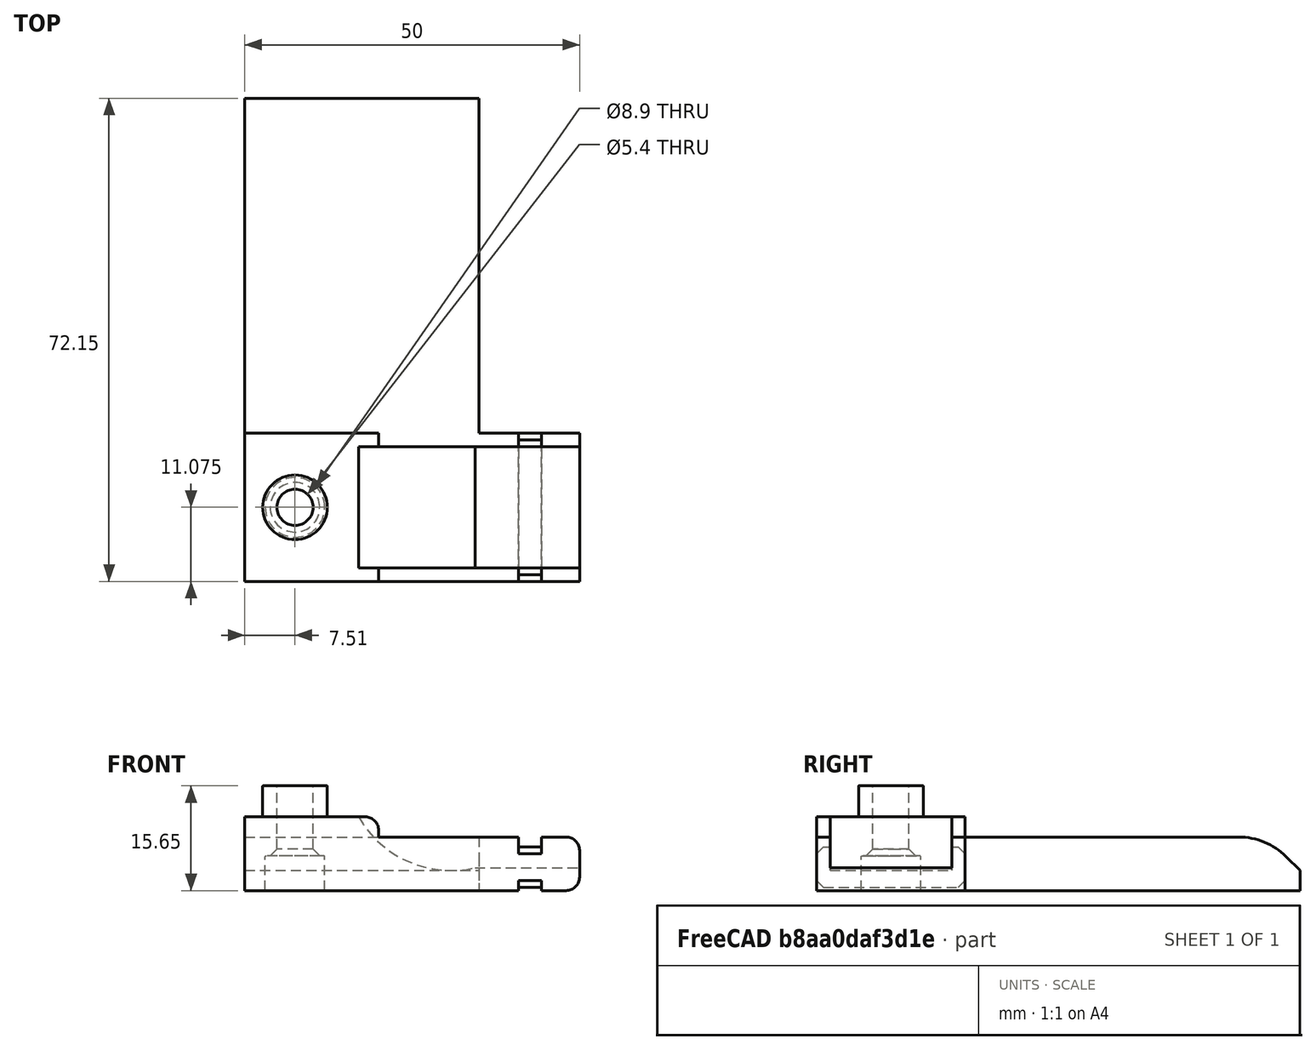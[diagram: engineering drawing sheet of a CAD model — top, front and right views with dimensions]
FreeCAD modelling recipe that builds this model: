
FCSTD DOCUMENT  (FreeCAD 0.19R24276 (Git))
Label: SoporteVelcroPowerBankCBR
License: All rights reserved
LicenseURL: http://en.wikipedia.org/wiki/All_rights_reserved
objects: TechDraw::DrawViewDimension×19, Part::Box×7, Part::MultiFuse×5, Part::Cylinder×4, Part::Offset×4, TechDraw::DrawProjGroupItem×3, Part::Cut×2, Part::Chamfer×2, Part::Fillet×2, TechDraw::DrawSVGTemplate×2, TechDraw::DrawViewPart×2, TechDraw::DrawPage×2, TechDraw::DrawProjGroup×1, TechDraw::DrawViewAnnotation×1
note: 26 computed .brp shape members not serialized (recipe doc carries the construction recipe); baked Part::Feature solids carry a one-line shape summary decoded from their .brp

FEATURE [Part::Cylinder] Cylinder
  Angle = 360
  AttacherType = Attacher::AttachEngine3D
  Height = 18.15
  Radius = 16
FEATURE [Part::Box] Box  label="Cube"
  AttacherType = Attacher::AttachEngine3D
  Height = 18.15
  Length = 17
  Placement = pos=(-30.835,0,0) rot=(0,0,1;0rad)
  Width = 8
FEATURE [Part::Box] Box001  label="Cube001"
  AttacherType = Attacher::AttachEngine3D
  Height = 18.15
  Length = 23
  Placement = pos=(3.4868,0,0) rot=(0,0,1;0rad)
  Width = 15.6
FEATURE [Part::Box] Box002  label="Cube002"
  AttacherType = Attacher::AttachEngine3D
  Height = 22.15
  Length = 50
  Placement = pos=(-30.84,11,-2) rot=(0,0,1;0rad)
  Width = 8
FEATURE [Part::Box] Box003  label="Cube003"
  AttacherType = Attacher::AttachEngine3D
  Height = 22.15
  Length = 20
  Placement = pos=(-30.84,8,-2) rot=(0,0,1;0rad)
  Width = 3
FEATURE [Part::Cylinder] Cylinder001
  Angle = 360
  AttacherType = Attacher::AttachEngine3D
  Height = 30
  Placement = pos=(-23.33,30,9.075) rot=(1,0,0;1.5708rad)
  Radius = 2.5
FEATURE [Part::Offset] Offset
  Fill = false
  Intersection = false
  Join = 0
  Mode = 0
  SelfIntersection = false
  Source = -> Cylinder001
  Value = 0.2
FEATURE [Part::MultiFuse] Fusion004
  Shapes = -> [Box002,Box003]
FEATURE [Part::Cylinder] Cylinder002
  Angle = 360
  AttacherType = Attacher::AttachEngine3D
  Height = 4.6
  Placement = pos=(-23.33,8,9.075) rot=(1,0,0;1.5708rad)
  Radius = 4.775
FEATURE [Part::Offset] Offset001
  Fill = false
  Intersection = false
  Join = 0
  Mode = 0
  SelfIntersection = false
  Source = -> Cylinder002
  Value = 0.05
FEATURE [Part::Offset] Offset002
  Fill = false
  Intersection = false
  Join = 0
  Mode = 0
  SelfIntersection = false
  Source = -> Cylinder002
  Value = 0.15
FEATURE [Part::Cut] Cut
  Base = -> Box
  Tool = -> Offset002
FEATURE [Part::Cylinder] Cylinder003
  Angle = 360
  AttacherType = Attacher::AttachEngine3D
  Height = 5
  Placement = pos=(-23.33,19,9.075) rot=(1,0,0;1.5708rad)
  Radius = 4.25
FEATURE [Part::Offset] Offset003
  Fill = false
  Intersection = false
  Join = 0
  Mode = 0
  SelfIntersection = false
  Source = -> Cylinder003
  Value = 0.2
FEATURE [Part::Box] Box005  label="Cube005"
  AttacherType = Attacher::AttachEngine3D
  Height = 50
  Length = 35
  Placement = pos=(-30.84,11,20.15) rot=(0,0,1;0rad)
  Width = 8
FEATURE [Part::Box] Box006  label="Cube006"
  AttacherType = Attacher::AttachEngine3D
  Height = 30
  Length = 3.45
  Placement = pos=(10.05,18.5,-6.425) rot=(0,0,1;0rad)
  Width = 2.45
FEATURE [Part::MultiFuse] Fusion
  Shapes = -> [Fusion004,Box005,Offset001]
FEATURE [Part::MultiFuse] Fusion006
  Shapes = -> [Offset003,Box006]
FEATURE [Part::Box] Box007  label="Cube007"
  AttacherType = Attacher::AttachEngine3D
  Height = 30
  Length = 3.45
  Placement = pos=(10.05,10.05,-6.425) rot=(0,0,1;0rad)
  Width = 2.45
FEATURE [Part::MultiFuse] Fusion007
  Shapes = -> [Offset,Cylinder,Box001,Cut,Box007]
FEATURE [Part::MultiFuse] Fusion008
  Shapes = -> [Fusion006,Fusion007]
FEATURE [Part::Cut] Cut001
  Base = -> Fusion
  Tool = -> Fusion008
FEATURE [Part::Chamfer] Chamfer
  Base = -> Cut001
  Edges = 1 edges r=5: [Edge8]
FEATURE [Part::Fillet] Fillet
  Base = -> Chamfer
  Edges = 1 edges r=10: [Edge7]
FEATURE [Part::Chamfer] Chamfer001
  Base = -> Fillet
  Edges = 5 edges r=1: [Edge38,Edge44,Edge49,Edge55,Edge117]
FEATURE [Part::Fillet] Fillet001
  Base = -> Chamfer001
  Edges = 5 edges r=2: [Edge26,Edge33,Edge37,Edge94,Edge103]
  Placement = pos=(0,0,0) rot=(-1,0,0;1.5708rad)
FEATURE [TechDraw::DrawSVGTemplate] Template
  EditableTexts = Designed_by_Name=<owner>; Drawing_number=001; FC-Date=-; FC-SC=1:1; FC-SH=1/2; FC-Title=PowerBankHolder; Subtitle=Soporte Bateria Externa; Weight=<250gr
  Height = 210
  Orientation = 1
  Width = 297
FEATURE [TechDraw::DrawSVGTemplate] Template001
  EditableTexts = Designed_by_Name=<owner>; Drawing_number=001; FC-Date=-; FC-SC=2/2; FC-SH=2/2; FC-Title=PowerBankHolder; Subtitle=Soporte Bateria Externa; Weight=<250gr
  Height = 210
  Orientation = 1
  Width = 297
FEATURE [TechDraw::DrawViewPart] View
  CoarseView = false
  Direction = (0.577,-0.577,0.577)
  Focus = 100
  HardHidden = false
  IsoCount = 0
  IsoHidden = false
  IsoVisible = false
  LockPosition = false
  Perspective = false
  Rotation = 0
  ScaleType = 0
  SeamHidden = false
  SeamVisible = true
  SmoothHidden = false
  SmoothVisible = true
  Source = -> [Fillet001]
  X = 230.5
  XDirection = (0.707,0.707,0)
  Y = 130.2
FEATURE [TechDraw::DrawViewPart] View001
  CoarseView = false
  Direction = (0.577,-0.577,0.577)
  Focus = 100
  HardHidden = false
  IsoCount = 0
  IsoHidden = false
  IsoVisible = false
  LockPosition = false
  Perspective = false
  Rotation = 0
  Scale = 2
  ScaleType = 0
  SeamHidden = false
  SeamVisible = true
  SmoothHidden = false
  SmoothVisible = true
  Source = -> [Fillet001]
  X = 154.004
  XDirection = (0.707,0.707,0)
  Y = 128.535
FEATURE [TechDraw::DrawProjGroupItem] ProjItem  label="Front"
  CoarseView = false
  Direction = (0,-1,0)
  Focus = 100
  HardHidden = false
  IsoCount = 0
  IsoHidden = false
  IsoVisible = false
  LockPosition = true
  Perspective = false
  Rotation = 0
  RotationVector = (1,0,0)
  ScaleType = 2
  SeamHidden = false
  SeamVisible = true
  SmoothHidden = false
  SmoothVisible = true
  Source = -> [Fillet001]
  Type = 0
  X = 0
  XDirection = (1,0,0)
  Y = 0
FEATURE [TechDraw::DrawProjGroupItem] ProjItem001  label="Right"
  CoarseView = false
  Direction = (1,-1e-16,0)
  Focus = 100
  HardHidden = false
  IsoCount = 0
  IsoHidden = false
  IsoVisible = false
  LockPosition = false
  Perspective = false
  Rotation = 0
  RotationVector = (1,0,0)
  ScaleType = 2
  SeamHidden = false
  SeamVisible = true
  SmoothHidden = false
  SmoothVisible = true
  Source = -> [Fillet001]
  Type = 2
  X = -87.15
  XDirection = (1e-16,1,0)
  Y = 0
FEATURE [TechDraw::DrawProjGroupItem] ProjItem002  label="Top"
  CoarseView = false
  Direction = (0,0,1)
  Focus = 100
  HardHidden = false
  IsoCount = 0
  IsoHidden = false
  IsoVisible = false
  LockPosition = false
  Perspective = false
  Rotation = 0
  RotationVector = (1,0,0)
  ScaleType = 2
  SeamHidden = false
  SeamVisible = true
  SmoothHidden = false
  SmoothVisible = true
  Source = -> [Fillet001]
  Type = 4
  X = 0
  XDirection = (1,0,0)
  Y = -69.75
FEATURE [TechDraw::DrawProjGroup] ProjGroup
  Anchor = -> ProjItem
  AutoDistribute = true
  LockPosition = false
  ProjectionType = 0
  Rotation = 0
  ScaleType = 0
  Source = -> [Fillet001]
  Views = -> [ProjItem,ProjItem001,ProjItem002]
  X = 140.1
  Y = 173.4
  spacingX = 15
  spacingY = 15
FEATURE [TechDraw::DrawViewDimension] Dimension
  Arbitrary = false
  ArbitraryTolerances = false
  EqualTolerance = true
  FormatSpec = %.2f
  FormatSpecOverTolerance = %+.2f
  FormatSpecUnderTolerance = %+.2f
  Inverted = false
  LockPosition = false
  MeasureType = 1
  OverTolerance = 0
  References2D = -> [ProjItem001]
  Rotation = 0
  ScaleType = 0
  TheoreticalExact = false
  Type = 1
  UnderTolerance = 0
  X = 3.6e-15
  Y = -7.825
FEATURE [TechDraw::DrawViewDimension] Dimension001
  Arbitrary = false
  ArbitraryTolerances = false
  EqualTolerance = true
  FormatSpec = %.2f
  FormatSpecOverTolerance = %+.2f
  FormatSpecUnderTolerance = %+.2f
  Inverted = false
  LockPosition = false
  MeasureType = 1
  OverTolerance = 0
  References2D = -> [ProjItem]
  Rotation = 0
  ScaleType = 0
  TheoreticalExact = false
  Type = 2
  UnderTolerance = 0
  X = -40.8017
  Y = 0.708725
FEATURE [TechDraw::DrawViewDimension] Dimension002
  Arbitrary = false
  ArbitraryTolerances = false
  EqualTolerance = true
  FormatSpec = %.2f
  FormatSpecOverTolerance = %+.2f
  FormatSpecUnderTolerance = %+.2f
  Inverted = false
  LockPosition = false
  MeasureType = 1
  OverTolerance = 0
  References2D = -> [ProjItem002]
  Rotation = 0
  ScaleType = 0
  TheoreticalExact = false
  Type = 1
  UnderTolerance = 0
  X = -3.24074
  Y = 46.4917
FEATURE [TechDraw::DrawPage] Page  label="Vistas"
  KeepUpdated = true
  NextBalloonIndex = 1
  ProjectionType = 0
  Template = -> Template
  Views = -> [View,ProjGroup,Dimension,Dimension001,Dimension002]
FEATURE [TechDraw::DrawViewDimension] Dimension003
  Arbitrary = false
  ArbitraryTolerances = false
  EqualTolerance = true
  FormatSpec = ⌀%.2f
  FormatSpecOverTolerance = %+.2f
  FormatSpecUnderTolerance = %+.2f
  Inverted = false
  LockPosition = false
  MeasureType = 1
  OverTolerance = 0
  References2D = -> [View001]
  Rotation = 0
  ScaleType = 0
  TheoreticalExact = false
  Type = 5
  UnderTolerance = 0
  X = 59.3366
  Y = 20.996
FEATURE [TechDraw::DrawViewDimension] Dimension004
  Arbitrary = false
  ArbitraryTolerances = false
  EqualTolerance = true
  FormatSpec = %.2f
  FormatSpecOverTolerance = %+.2f
  FormatSpecUnderTolerance = %+.2f
  Inverted = false
  LockPosition = false
  MeasureType = 1
  OverTolerance = 0
  References2D = -> [View001]
  Rotation = 0
  ScaleType = 0
  TheoreticalExact = false
  Type = 2
  UnderTolerance = 0
  X = -102.544
  Y = 1.17066
FEATURE [TechDraw::DrawViewDimension] Dimension005
  Arbitrary = false
  ArbitraryTolerances = false
  EqualTolerance = true
  FormatSpec = ⌀%.2f
  FormatSpecOverTolerance = %+.2f
  FormatSpecUnderTolerance = %+.2f
  Inverted = false
  LockPosition = false
  MeasureType = 1
  OverTolerance = 0
  References2D = -> [View001]
  Rotation = 0
  ScaleType = 0
  TheoreticalExact = false
  Type = 5
  UnderTolerance = 0
  X = -48.9907
  Y = 41.3835
FEATURE [TechDraw::DrawViewDimension] Dimension006
  Arbitrary = false
  ArbitraryTolerances = false
  EqualTolerance = true
  FormatSpec = ⌀%.2f
  FormatSpecOverTolerance = %+.2f
  FormatSpecUnderTolerance = %+.2f
  Inverted = false
  LockPosition = false
  MeasureType = 1
  OverTolerance = 0
  References2D = -> [View001]
  Rotation = 0
  ScaleType = 0
  TheoreticalExact = false
  Type = 5
  UnderTolerance = 0
  X = -74.5511
  Y = 34.3848
FEATURE [TechDraw::DrawViewDimension] Dimension007
  Arbitrary = false
  ArbitraryTolerances = false
  EqualTolerance = true
  FormatSpec = ⌀%.2f
  FormatSpecOverTolerance = %+.2f
  FormatSpecUnderTolerance = %+.2f
  Inverted = false
  LockPosition = false
  MeasureType = 1
  OverTolerance = 0
  References2D = -> [View001]
  Rotation = 0
  ScaleType = 0
  TheoreticalExact = false
  Type = 5
  UnderTolerance = 0
  X = -0.912871
  Y = 27.3861
FEATURE [TechDraw::DrawViewDimension] Dimension008
  Arbitrary = false
  ArbitraryTolerances = false
  EqualTolerance = true
  FormatSpec = ⌀%.2f
  FormatSpecOverTolerance = %+.2f
  FormatSpecUnderTolerance = %+.2f
  Inverted = false
  LockPosition = false
  MeasureType = 1
  OverTolerance = 0
  References2D = -> [View001]
  Rotation = 0
  ScaleType = 0
  TheoreticalExact = false
  Type = 5
  UnderTolerance = 0
  X = 29.7389
  Y = -10.4488
FEATURE [TechDraw::DrawViewDimension] Dimension009
  Arbitrary = false
  ArbitraryTolerances = false
  EqualTolerance = true
  FormatSpec = %.2f
  FormatSpecOverTolerance = %+.2f
  FormatSpecUnderTolerance = %+.2f
  Inverted = false
  LockPosition = false
  MeasureType = 1
  OverTolerance = 0
  References2D = -> [View001]
  Rotation = 0
  ScaleType = 0
  TheoreticalExact = false
  Type = 0
  UnderTolerance = 0
  X = 31.4456
  Y = -35.2254
FEATURE [TechDraw::DrawViewDimension] Dimension010
  Arbitrary = false
  ArbitraryTolerances = false
  EqualTolerance = true
  FormatSpec = ⌀%.2f
  FormatSpecOverTolerance = %+.2f
  FormatSpecUnderTolerance = %+.2f
  Inverted = false
  LockPosition = false
  MeasureType = 1
  OverTolerance = 0
  References2D = -> [View001]
  Rotation = 0
  ScaleType = 0
  TheoreticalExact = false
  Type = 5
  UnderTolerance = 0
  X = -32.954
  Y = -8.1983
FEATURE [TechDraw::DrawViewDimension] Dimension011
  Arbitrary = false
  ArbitraryTolerances = false
  EqualTolerance = true
  FormatSpec = %.2f
  FormatSpecOverTolerance = %+.2f
  FormatSpecUnderTolerance = %+.2f
  Inverted = false
  LockPosition = false
  MeasureType = 1
  OverTolerance = 0
  References2D = -> [View001]
  Rotation = 0
  ScaleType = 0
  TheoreticalExact = false
  Type = 2
  UnderTolerance = 0
  X = -46.3901
  Y = -36.6465
FEATURE [TechDraw::DrawViewDimension] Dimension012
  Arbitrary = false
  ArbitraryTolerances = false
  EqualTolerance = true
  FormatSpec = %.2f
  FormatSpecOverTolerance = %+.2f
  FormatSpecUnderTolerance = %+.2f
  Inverted = false
  LockPosition = false
  MeasureType = 1
  OverTolerance = 0
  References2D = -> [View001]
  Rotation = 0
  ScaleType = 0
  TheoreticalExact = false
  Type = 0
  UnderTolerance = 0
  X = -26.0543
  Y = -49.0718
FEATURE [TechDraw::DrawViewDimension] Dimension013
  Arbitrary = false
  ArbitraryTolerances = false
  EqualTolerance = true
  FormatSpec = %.2f
  FormatSpecOverTolerance = %+.2f
  FormatSpecUnderTolerance = %+.2f
  Inverted = false
  LockPosition = false
  MeasureType = 1
  OverTolerance = 0
  References2D = -> [View001]
  Rotation = 0
  ScaleType = 0
  TheoreticalExact = false
  Type = 0
  UnderTolerance = 0
  X = -97.6121
  Y = 42.4551
FEATURE [TechDraw::DrawViewDimension] Dimension014
  Arbitrary = false
  ArbitraryTolerances = false
  EqualTolerance = true
  FormatSpec = %.2f
  FormatSpecOverTolerance = %+.2f
  FormatSpecUnderTolerance = %+.2f
  Inverted = false
  LockPosition = false
  MeasureType = 1
  OverTolerance = 0
  References2D = -> [View001]
  Rotation = 0
  ScaleType = 0
  TheoreticalExact = false
  Type = 2
  UnderTolerance = 0
  X = 82.6342
  Y = 18.2959
FEATURE [TechDraw::DrawViewDimension] Dimension015
  Arbitrary = false
  ArbitraryTolerances = false
  EqualTolerance = true
  FormatSpec = %.2f
  FormatSpecOverTolerance = %+.2f
  FormatSpecUnderTolerance = %+.2f
  Inverted = false
  LockPosition = false
  MeasureType = 1
  OverTolerance = 0
  References2D = -> [View001]
  Rotation = 0
  ScaleType = 0
  TheoreticalExact = false
  Type = 2
  UnderTolerance = 0
  X = -3.06494
  Y = -31.7723
FEATURE [TechDraw::DrawViewDimension] Dimension016
  Arbitrary = false
  ArbitraryTolerances = false
  EqualTolerance = true
  FormatSpec = %.2f
  FormatSpecOverTolerance = %+.2f
  FormatSpecUnderTolerance = %+.2f
  Inverted = false
  LockPosition = false
  MeasureType = 1
  OverTolerance = 0
  References2D = -> [View001]
  Rotation = 0
  ScaleType = 0
  TheoreticalExact = false
  Type = 0
  UnderTolerance = 0
  X = 35.3454
  Y = 5.33411
FEATURE [TechDraw::DrawViewDimension] Dimension017
  Arbitrary = false
  ArbitraryTolerances = false
  EqualTolerance = true
  FormatSpec = %.2f
  FormatSpecOverTolerance = %+.2f
  FormatSpecUnderTolerance = %+.2f
  Inverted = false
  LockPosition = false
  MeasureType = 1
  OverTolerance = 0
  References2D = -> [View001]
  Rotation = 0
  ScaleType = 0
  TheoreticalExact = false
  Type = 2
  UnderTolerance = 0
  X = -74.6491
  Y = -19.0944
FEATURE [TechDraw::DrawViewDimension] Dimension018
  Arbitrary = false
  ArbitraryTolerances = false
  EqualTolerance = true
  FormatSpec = ⌀%.2f
  FormatSpecOverTolerance = %+.2f
  FormatSpecUnderTolerance = %+.2f
  Inverted = false
  LockPosition = false
  MeasureType = 1
  OverTolerance = 0
  References2D = -> [View001]
  Rotation = 0
  ScaleType = 0
  TheoreticalExact = false
  Type = 5
  UnderTolerance = 0
  X = 10.5893
  Y = -52.2162
FEATURE [TechDraw::DrawViewAnnotation] Annotation
  Font = osifont
  LineSpace = 80
  LockPosition = false
  MaxWidth = -1
  Rotation = 0
  ScaleType = 0
  Text = Aproximate measurements: | Check with 3D piece
  TextSize = 5
  TextStyle = 0
  X = 63.7
  Y = 54.6
FEATURE [TechDraw::DrawPage] Page001  label="Cotas"
  KeepUpdated = true
  NextBalloonIndex = 1
  ProjectionType = 0
  Template = -> Template001
  Views = -> [View001,Dimension003,Dimension004,Dimension005,Dimension006,Dimension007,Dimension008,Dimension009,Dimension010,Dimension011,Dimension012,Dimension013,Dimension014,Dimension015,Dimension016,Dimension017,Dimension018,Annotation]
